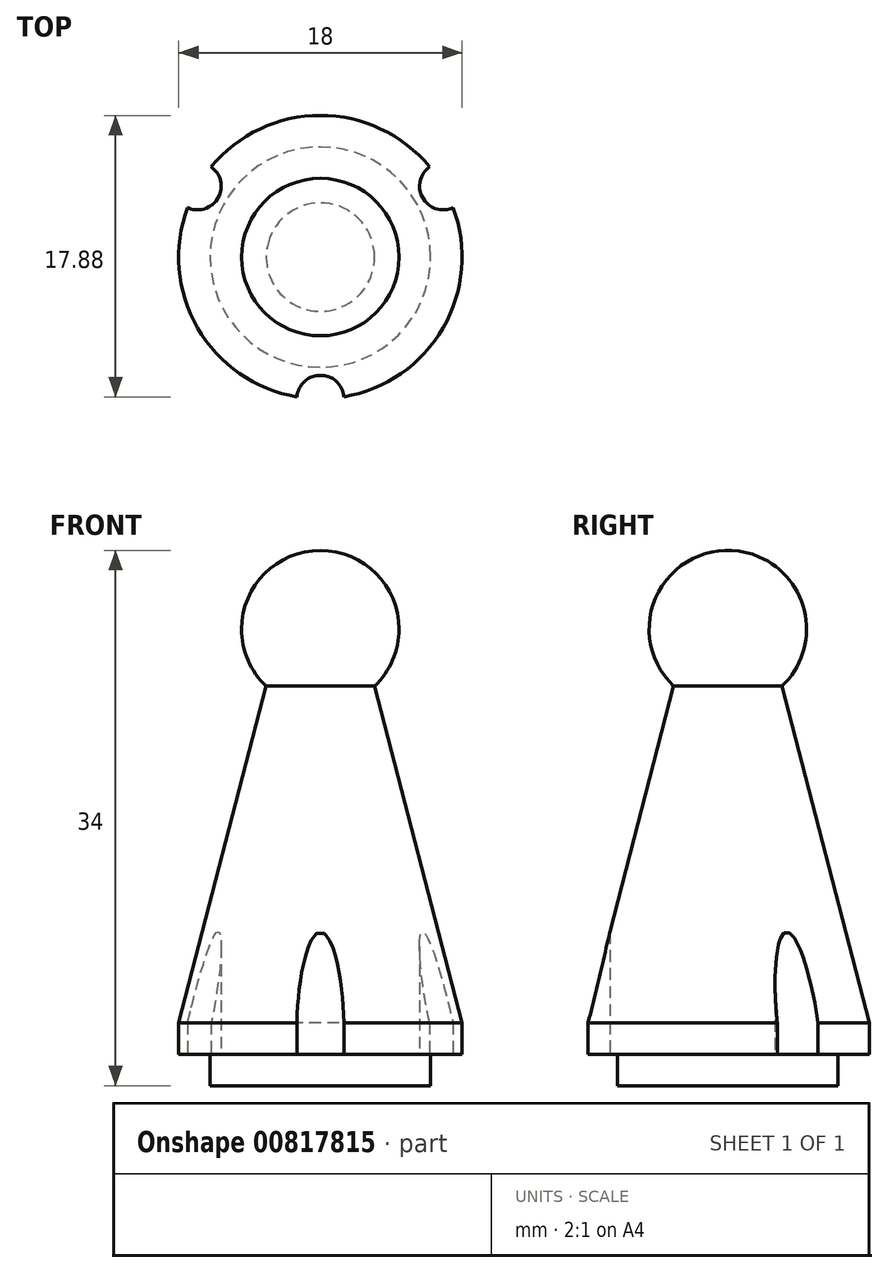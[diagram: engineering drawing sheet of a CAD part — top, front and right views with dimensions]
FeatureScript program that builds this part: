
annotation { "Feature Type Name" : "Feature", "Feature Type Description" : "" }
export const myFeature = defineFeature(function(context is Context, id is Id, definition is map)
    precondition{}
    {
        {
            var Q0;
            Q0=qCreatedBy(makeId("Top.planeOp"),FACE);
            var sketch = newSketch(context, id + "F0", { "sketchPlane" : qUnion([Q0])});
            skCircle(sketch, "E0", {"center": v(0, 0) * mm, "radius": 7 * mm});
            skSolve(sketch);
        }
        {
            var Q0;
            Q0=makeQuery(id+"F0.imprint","IMPRINT",FACE,{"disambiguationData":[TD([[makeQuery(id+"F0.imprint","IMPRINT",EDGE,{"derivedFrom":sQuery(id+"F0.wireOp",EDGE,"E0")}),1.0]])]});
            extrude(context, id + "F1", {"entities" : qUnion([Q0]), "depth" : 2 * mm, "offsetDistance" : 25 * mm});
        }
        {
            var Q0;
            Q0=makeQuery(id+"F1.opExtrude","CAP_FACE",FACE,{"disambiguationData":[OSD([sQuery(id+"F0.wireOp",EDGE,"E0")])],"isStart":false});
            var sketch = newSketch(context, id + "F2", { "sketchPlane" : qUnion([Q0])});
            skCircle(sketch, "E1", {"center": v(0, 0) * mm, "radius": 9 * mm});
            skSolve(sketch);
        }
        {
            var Q0;
            Q0 = qSketchRegion(id + "F2", true);
            extrude(context, id + "F3", {"entities" : qUnion([Q0]), "operationType" : NewBodyOperationType.ADD, "depth" : 2 * mm, "offsetDistance" : 25 * mm});
        }
        {
            var Q0;
            Q0=makeQuery(id+"F3.opExtrude","CAP_FACE",FACE,{"disambiguationData":[OSD([sQuery(id+"F2.wireOp",EDGE,"E1")])],"isStart":false});
            cPlane(context, id + "F4", {"entities" : qUnion([Q0]), "cplaneType" : CPlaneType.OFFSET, "offset" : 25 * mm, "width" : 150 * mm, "height" : 150 * mm});
        }
        {
            var Q0;
            Q0=qCreatedBy(id+"F4.planeOp",FACE);
            var sketch = newSketch(context, id + "F5", { "sketchPlane" : qUnion([Q0])});
            skCircle(sketch, "E2", {"center": v(0, 0) * mm, "radius": 2.5 * mm});
            skSolve(sketch);
        }
        {
            var Q1;
            Q1=makeQuery(id+"F3.opExtrude","CAP_FACE",FACE,{"disambiguationData":[OSD([sQuery(id+"F2.wireOp",EDGE,"E1")])],"isStart":false});
            var Q2;
            Q2=makeQuery(id+"F5.imprint","IMPRINT",FACE,{"disambiguationData":[TD([[makeQuery(id+"F5.imprint","IMPRINT",EDGE,{"derivedFrom":sQuery(id+"F5.wireOp",EDGE,"E2")}),1.0]])]});
            loft(context, id + "F6", {"operationType" : NewBodyOperationType.ADD, "sheetProfilesArray" : [{ "sheetProfileEntities" : qUnion([Q1]) }, { "sheetProfileEntities" : qUnion([Q2]) }]});
        }
        {
            var Q0;
            Q0=makeQuery(id+"F6.opLoft","CAP_FACE",FACE,{"disambiguationData":[OSD([makeQuery(id+"F5.imprint","IMPRINT",FACE,{"disambiguationData":[TD([[makeQuery(id+"F5.imprint","IMPRINT",EDGE,{"derivedFrom":sQuery(id+"F5.wireOp",EDGE,"E2")}),1.0]])]})])],"isStart":true});
            var sketch = newSketch(context, id + "F7", { "sketchPlane" : qUnion([Q0])});
            skCircle(sketch, "E3", {"center": v(0, 0) * mm, "radius": 5 * mm});
            skLineSegment(sketch, "E4", {"start": v(-5, 0) * mm, "end": v(5, 0) * mm});
            skSolve(sketch);
        }
        {
            var Q0;
            {var subQ0=sQuery(id+"F7.wireOp",EDGE,"E4");var subQ1=sQuery(id+"F7.wireOp",EDGE,"E3");var subQ2=makeQuery(id+"F7.imprint","INTERSECT",VERTEX,{"disambiguationData":[OD(0.0)],"derivedFrom":[subQ1,subQ0]});Q0=makeQuery(id+"F7.imprint","IMPRINT",FACE,{"disambiguationData":[TD([[makeQuery(id+"F7.imprint","IMPRINT",EDGE,{"disambiguationData":[TD([[subQ2,1.0]])],"derivedFrom":subQ1}),1.0]])]});}
            var Q1;
            {var subQ0=sQuery(id+"F7.wireOp",EDGE,"E4");var subQ1=makeQuery(id+"F6.opLoft","MID_CAP_EDGE",EDGE,{"disambiguationData":[OSD([sQuery(id+"F5.wireOp",EDGE,"E2")])],"capPos":1.0});var subQ2=makeQuery(id+"F7.imprint","INTERSECT",VERTEX,{"disambiguationData":[OD(0.0)],"derivedFrom":[subQ1,subQ0]});Q1=makeQuery(id+"F7.imprint","IMPRINT",FACE,{"disambiguationData":[TD([[makeQuery(id+"F7.imprint","IMPRINT",EDGE,{"disambiguationData":[TD([[subQ2,-1.0]])],"derivedFrom":subQ0}),1.0]])]});}
            var Q2;
            Q2=sQuery(id+"F7.wireOp",EDGE,"E4");
            revolve(context, id + "F8", {"operationType" : NewBodyOperationType.ADD, "surfaceOperationType" : NewSurfaceOperationType.NEW, "entities" : qUnion([Q0, Q1]), "axis" : qUnion([Q2]), "revolveType" : RevolveType.FULL});
        }
        {
            var Q0;
            Q0=makeQuery(id+"F3.opExtrude","CAP_FACE",FACE,{"disambiguationData":[OSD([sQuery(id+"F2.wireOp",EDGE,"E1")])],"isStart":true});
            var sketch = newSketch(context, id + "F9", { "sketchPlane" : qUnion([Q0])});
            skCircle(sketch, "E5", {"center": v(0, 9) * mm, "radius": 1.5 * mm});
            skCircle(sketch, "E6.1.0", {"center": v(-7.8, -4.5) * mm, "radius": 1.5 * mm});
            skCircle(sketch, "E6.2.0", {"center": v(7.8, -4.5) * mm, "radius": 1.5 * mm});
            skPoint(sketch, "E6.center", {"position": v(0, 0) * mm});
            skSolve(sketch);
        }
        {
            var Q0;
            Q0 = qSketchRegion(id + "F9", true);
            extrude(context, id + "F10", {"entities" : qUnion([Q0]), "operationType" : NewBodyOperationType.REMOVE, "endBound" : BoundingType.THROUGH_ALL, "oppositeDirection" : true, "depth" : 25 * mm, "offsetDistance" : 25 * mm});
        }
    });
